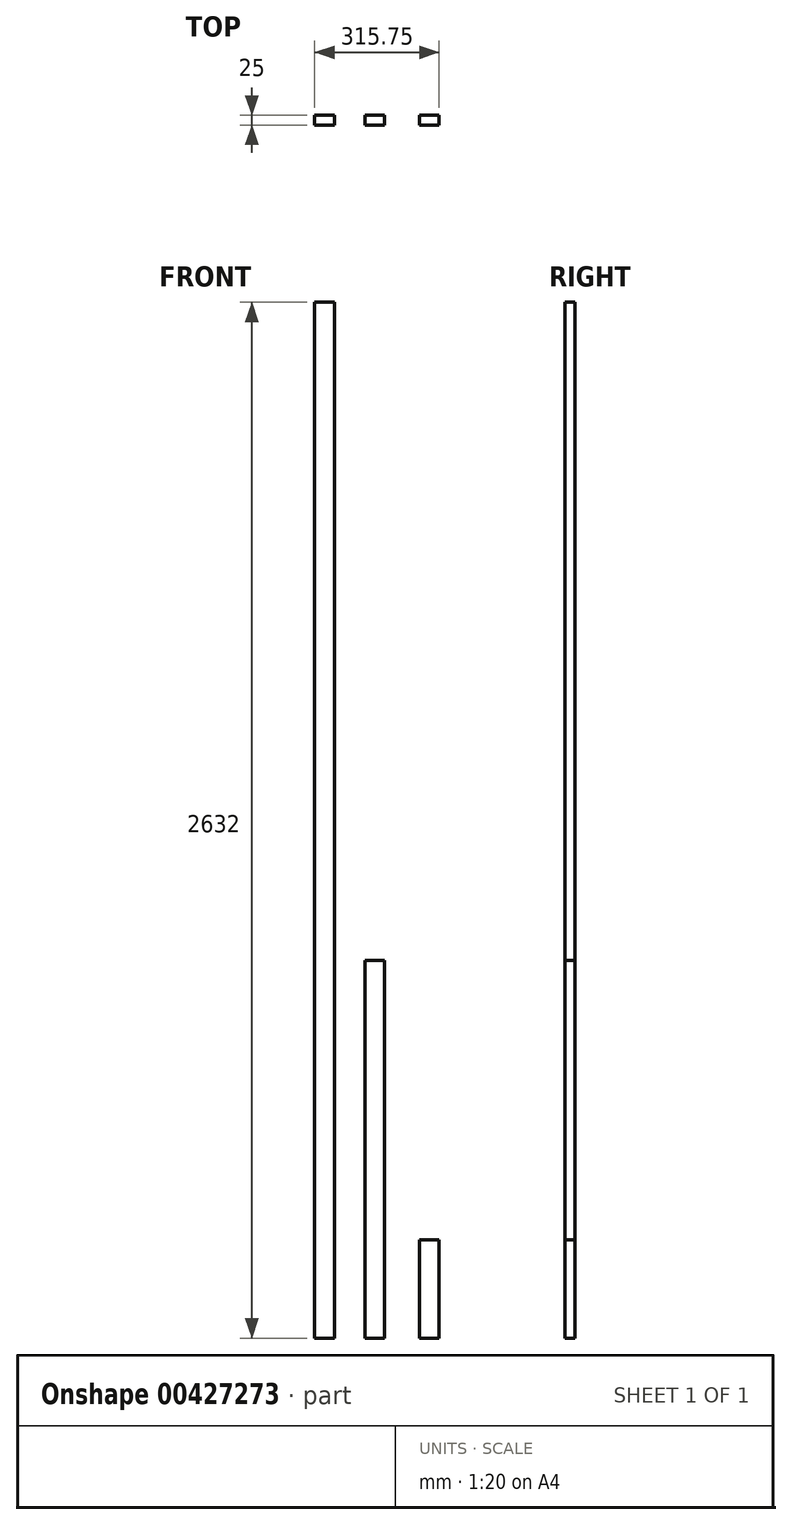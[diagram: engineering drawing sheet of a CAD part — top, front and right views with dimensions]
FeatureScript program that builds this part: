
annotation { "Feature Type Name" : "Feature", "Feature Type Description" : "" }
export const myFeature = defineFeature(function(context is Context, id is Id, definition is map)
    precondition{}
    {
        {
            var Q0;
            Q0=qCreatedBy(makeId("Front.planeOp"),FACE);
            var sketch = newSketch(context, id + "F0", { "sketchPlane" : qUnion([Q0])});
            skLineSegment(sketch, "E0.bottom", {"start": v(0, 0) * mm, "end": v(50, 0) * mm});
            skLineSegment(sketch, "E0.top", {"start": v(0, 2632) * mm, "end": v(50, 2632) * mm});
            skLineSegment(sketch, "E0.left", {"start": v(0, 0) * mm, "end": v(0, 2632) * mm});
            skLineSegment(sketch, "E0.right", {"start": v(50, 0) * mm, "end": v(50, 2632) * mm});
            skSolve(sketch);
        }
        {
            var Q0;
            Q0=makeQuery(id+"F0.imprint","IMPRINT",FACE,{"disambiguationData":[TD([[makeQuery(id+"F0.imprint","IMPRINT",EDGE,{"derivedFrom":sQuery(id+"F0.wireOp",EDGE,"E0.bottom")}),1.0]])]});
            extrude(context, id + "F1", {"entities" : qUnion([Q0]), "depth" : 25 * mm, "offsetDistance" : 25 * mm});
        }
        {
            var Q0;
            Q0=qCreatedBy(makeId("Front.planeOp"),FACE);
            var sketch = newSketch(context, id + "F2", { "sketchPlane" : qUnion([Q0])});
            skLineSegment(sketch, "E1.bottom", {"start": v(127.67, 0) * mm, "end": v(177.67, 0) * mm});
            skLineSegment(sketch, "E1.top", {"start": v(127.67, 960) * mm, "end": v(177.67, 960) * mm});
            skLineSegment(sketch, "E1.left", {"start": v(127.67, 0) * mm, "end": v(127.67, 960) * mm});
            skLineSegment(sketch, "E1.right", {"start": v(177.67, 0) * mm, "end": v(177.67, 960) * mm});
            skSolve(sketch);
        }
        {
            var Q0;
            Q0 = qSketchRegion(id + "F2", true);
            extrude(context, id + "F3", {"entities" : qUnion([Q0]), "depth" : 25 * mm, "offsetDistance" : 25 * mm});
        }
        {
            var Q0;
            Q0=qCreatedBy(makeId("Front.planeOp"),FACE);
            var sketch = newSketch(context, id + "F4", { "sketchPlane" : qUnion([Q0])});
            skLineSegment(sketch, "E2.bottom", {"start": v(265.75, 0) * mm, "end": v(315.75, 0) * mm});
            skLineSegment(sketch, "E2.top", {"start": v(265.75, 250) * mm, "end": v(315.75, 250) * mm});
            skLineSegment(sketch, "E2.left", {"start": v(265.75, 0) * mm, "end": v(265.75, 250) * mm});
            skLineSegment(sketch, "E2.right", {"start": v(315.75, 0) * mm, "end": v(315.75, 250) * mm});
            skSolve(sketch);
        }
        {
            var Q0;
            Q0 = qSketchRegion(id + "F4", true);
            extrude(context, id + "F5", {"entities" : qUnion([Q0]), "depth" : 25 * mm, "offsetDistance" : 25 * mm});
        }
    });
